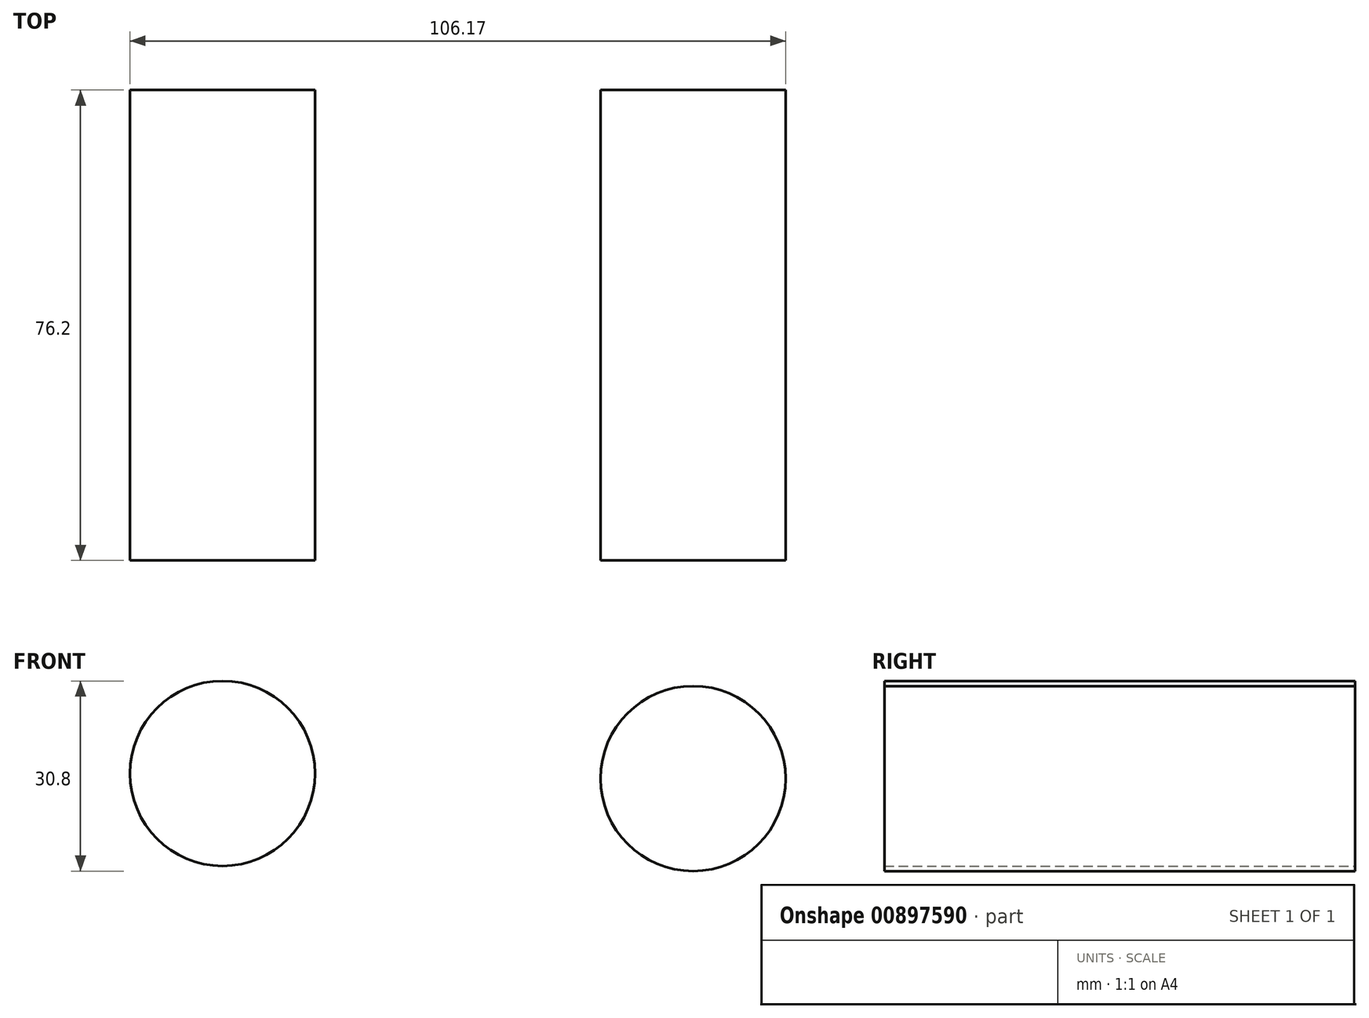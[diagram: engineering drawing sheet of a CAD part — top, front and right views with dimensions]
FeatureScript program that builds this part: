
annotation { "Feature Type Name" : "Feature", "Feature Type Description" : "" }
export const myFeature = defineFeature(function(context is Context, id is Id, definition is map)
    precondition{}
    {
        {
            var Q0;
            Q0=qCreatedBy(makeId("Front.planeOp"),FACE);
            var sketch = newSketch(context, id + "F0", { "sketchPlane" : qUnion([Q0])});
            skLineSegment(sketch, "E0", {"start": v(0, -44.76) * mm, "end": v(0, 55.9) * mm});
            skCircle(sketch, "E1", {"center": v(-47.97, 27.63) * mm, "radius": 14.99 * mm});
            skCircle(sketch, "E2.1.0.0", {"center": v(28.22, 26.8) * mm, "radius": 14.99 * mm});
            skLineSegment(sketch, "E2.direction1", {"start": v(-47.97, 27.63) * mm, "end": v(28.22, 26.8) * mm, "construction": true});
            skSolve(sketch);
        }
        {
            var Q0;
            Q0=makeQuery(id+"F0.imprint","IMPRINT",FACE,{"disambiguationData":[TD([[makeQuery(id+"F0.imprint","IMPRINT",EDGE,{"derivedFrom":sQuery(id+"F0.wireOp",EDGE,"E1")}),1.0]])]});
            var Q1;
            Q1=makeQuery(id+"F0.imprint","IMPRINT",FACE,{"disambiguationData":[TD([[makeQuery(id+"F0.imprint","IMPRINT",EDGE,{"derivedFrom":sQuery(id+"F0.wireOp",EDGE,"E2.1.0.0")}),1.0]])]});
            extrude(context, id + "F1", {"entities" : qUnion([Q0, Q1]), "depth" : 76.2 * mm, "offsetDistance" : 25.4 * mm});
        }
    });
